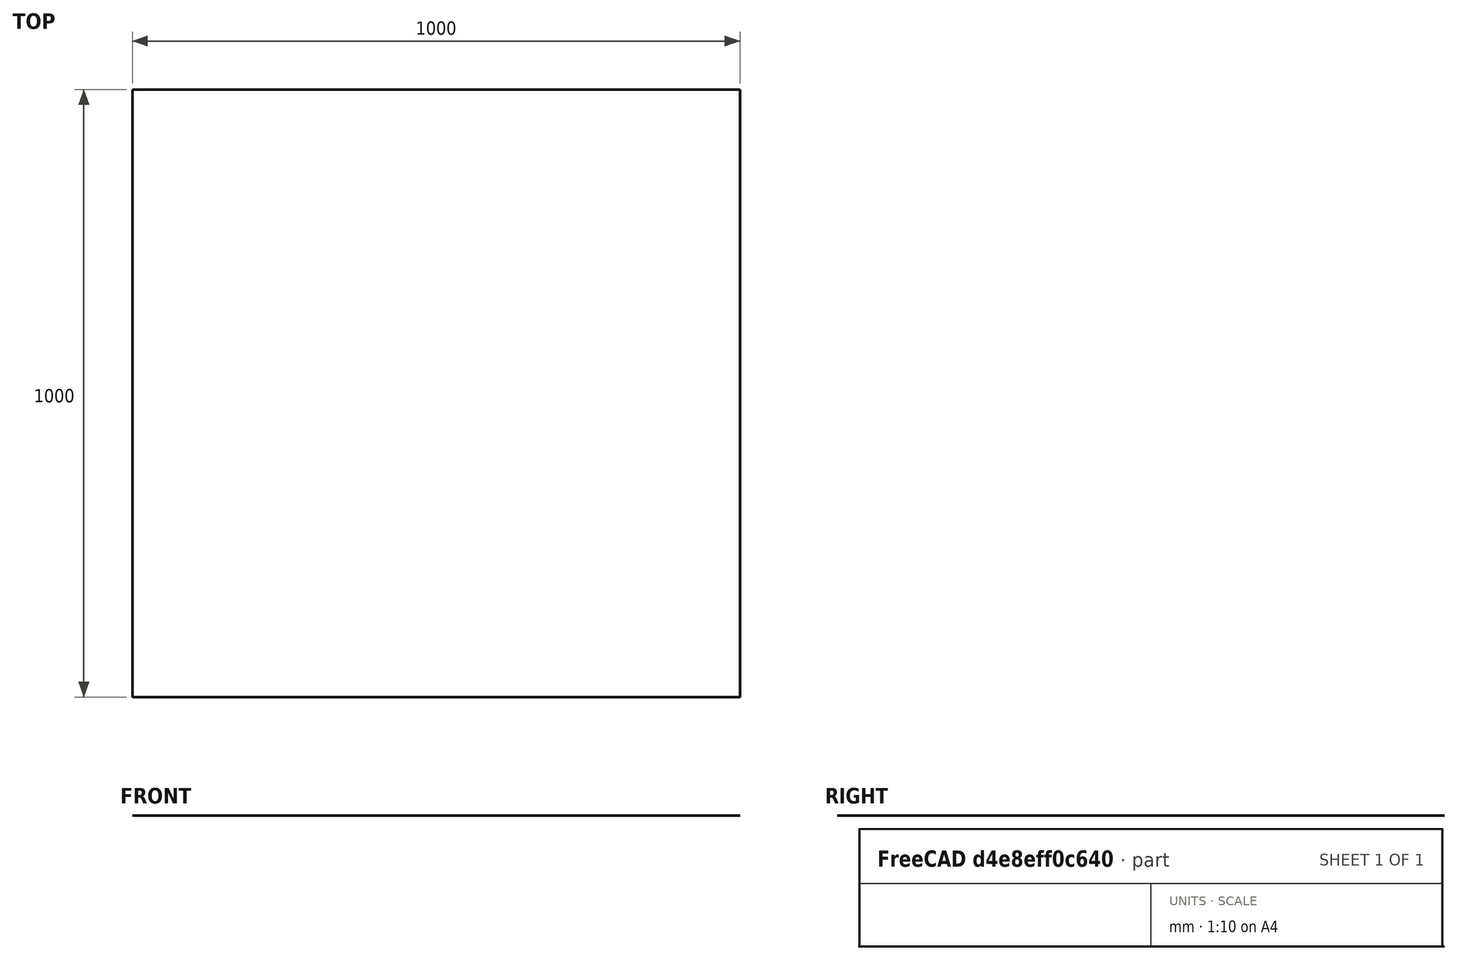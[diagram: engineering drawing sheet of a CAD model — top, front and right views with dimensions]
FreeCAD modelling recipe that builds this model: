
FCSTD DOCUMENT  (FreeCAD 0.17R11114 (Git))
Label: fridge_box
License: All rights reserved
LicenseURL: http://en.wikipedia.org/wiki/All_rights_reserved
objects: TechDraw::DrawViewDimension×26, Part::Part2DObjectPython×7, TechDraw::DrawViewDraft×4, Part::FeaturePython×3, TechDraw::DrawViewPart×3, Part::Compound×2, Part::Feature×2, TechDraw::DrawViewAnnotation×2, TechDraw::DrawSVGTemplate×1, App::DocumentObjectGroup×1, App::FeaturePython×1, TechDraw::DrawViewArch×1, App::DocumentObjectGroupPython×1, TechDraw::DrawPage×1
note: 15 computed .brp shape members not serialized (recipe doc carries the construction recipe); baked Part::Feature solids carry a one-line shape summary decoded from their .brp

FEATURE [Part::FeaturePython] fridge_box_door_01  # a2plus imported part (geometry in sourceFile) (typed FeaturePython)
  Placement = pos=(0,1e-12,0) rot=(0,0,1;0rad)
  fixedPosition = true
  sourceFile = fridge_box_door.fcstd
  timeLastImport = 1.49385e+09
  updateColors = true
FEATURE [Part::FeaturePython] fridge_box_panels_01  # a2plus imported part (geometry in sourceFile) (typed FeaturePython)
  fixedPosition = false
  sourceFile = A711_fridge_box_panels.fcstd
  timeLastImport = 1.49382e+09
  updateColors = true
FEATURE [Part::Compound] Compound
  Links = -> [fridge_box_door_01,fridge_box_panels_01]
FEATURE [TechDraw::DrawSVGTemplate] Template
  EditableTexts = 5cm_scaled_value=25cm; Architect_2=MARZIA FILATRELLA; Architect_3=MARCO FERRARA; Board_no=A712; Date=4.5.2017; Date_1=4.5.2017; Drawing_title_2=BOX FRIGO; Drawing_title_3=DISEGNI GENERALI; Filename=FRIDGE_BOX.FCSTD; Project_title_2=CASA VACANZE; Project_title_3=A SESTRI; Project_title_4=SCALA INTERNA; Revision=1.0; Scale=1:5; Sheet_of_sheets=3 DI 7 (nd); Size=A2; Version_1=1.0
  Height = 594
  Orientation = 0
  Width = 420
FEATURE [Part::Feature] Compound_cs  label="cs_hor_section"
  shape: bbox 610 x 720 x 3e-07 mm, 0 faces, 0 solids (baked)
FEATURE [Part::FeaturePython] fridge_box_door_02  # a2plus imported part (geometry in sourceFile) (typed FeaturePython)
  Placement = pos=(1865,1133,0) rot=(0,0,-1;1.5708rad)
  fixedPosition = false
  sourceFile = fridge_box_door.fcstd
  timeLastImport = 1.49385e+09
  updateColors = true
FEATURE [Part::Part2DObjectPython] Shape2DView001  # Draft 2D object (typed FeaturePython)
  Base = -> fridge_box_door_01
  FaceNumbers = [5]
  HiddenLines = false
  InPlace = true
  Projection = (0,0,1)
  ProjectionMode = 0
  SegmentLength = 0.05
  Tessellation = false
FEATURE [Part::Part2DObjectPython] Shape2DView  # Draft 2D object (typed FeaturePython)
  Base = -> fridge_box_door_02
  HiddenLines = false
  InPlace = true
  Projection = (0,0,1)
  ProjectionMode = 0
  SegmentLength = 0.05
  Tessellation = false
FEATURE [Part::Part2DObjectPython] Arc  # Draft 2D object (typed FeaturePython)
  FirstAngle = -90
  LastAngle = 0
  MakeFace = true
  Placement = pos=(1490,-357,0) rot=(0,0,1;0rad)
  Radius = 610
FEATURE [Part::Compound] Compound001  label="door_opening"
  Links = -> [Shape2DView001,Shape2DView,Arc]
FEATURE [App::DocumentObjectGroup] Group  label="utilities"
  Group = -> [fridge_box_door_02]
FEATURE [App::FeaturePython] Section  label="pl_hor_section"  # WARN: FeaturePython — macro-defined, semantics opaque (R4)
  Objects = -> [Compound]
  OnlySolids = true
  Placement = pos=(1810.65,0,1000) rot=(0,0,1;0rad)
FEATURE [TechDraw::DrawViewPart] View  label="plan"
  ArcCenterMarks = true
  CenterScale = 2
  Direction = (0,0,1)
  HardHidden = true
  HiddenWidth = 0.15
  HorizCenterLine = false
  IsoCount = 0
  IsoHidden = false
  IsoVisible = false
  IsoWidth = 0.3
  KeepLabel = false
  LineWidth = 0.5
  Rotation = 0
  Scale = 0.2
  ScaleType = 2
  SeamHidden = false
  SeamVisible = false
  ShowSectionLine = true
  SmoothHidden = false
  SmoothVisible = false
  Source = -> Compound_cs
  VertCenterLine = false
  X = 100
  Y = 275
FEATURE [TechDraw::DrawViewPart] View001  label="opening"
  ArcCenterMarks = true
  CenterScale = 2
  Direction = (0,0,1)
  HardHidden = false
  HiddenWidth = 0.15
  HorizCenterLine = false
  IsoCount = 0
  IsoHidden = false
  IsoVisible = false
  IsoWidth = 0.3
  KeepLabel = false
  LineWidth = 0.1
  Rotation = 0
  Scale = 0.2
  ScaleType = 2
  SeamHidden = false
  SeamVisible = false
  ShowSectionLine = true
  SmoothHidden = false
  SmoothVisible = false
  Source = -> Compound001
  VertCenterLine = false
  X = 100
  Y = 145.6
  expr: Y = View.Y - 2 * 64.700000000000003
  expr: X = View.X
FEATURE [TechDraw::DrawViewArch] ArchView  label="plan_all"
  AllOn = true
  FontSize = 12
  KeepLabel = false
  LineWidth = 0.05
  RenderMode = 0
  Rotation = 0
  Scale = 0.2
  ScaleType = 2
  ShowFill = false
  ShowHidden = true
  Source = -> Section
  Symbol = <blob: 2967 chars omitted>
  X = 35
  Y = 347.2
  expr: Y = View.Y + 2 * 36.100000000000001
  expr: X = View.X - 2 * 32.5
FEATURE [TechDraw::DrawViewDimension] Dimension
  Font = Arial
  Fontsize = 3
  FormatSpec = %value%
  KeepLabel = false
  LineWidth = 0.1
  MeasureType = 1
  References2D = -> [View]
  Rotation = 0
  ScaleType = 0
  Type = 2
  X = -48.5904
  Y = -6.90054
FEATURE [TechDraw::DrawViewDimension] Dimension001
  Font = Arial
  Fontsize = 3
  FormatSpec = %value%
  KeepLabel = false
  LineWidth = 0.1
  MeasureType = 1
  References2D = -> [View]
  Rotation = 0
  ScaleType = 0
  Type = 1
  X = 0.98199
  Y = -50.7245
FEATURE [TechDraw::DrawViewDimension] Dimension002
  Font = Arial
  Fontsize = 3
  FormatSpec = %value%
  KeepLabel = false
  LineWidth = 0.1
  MeasureType = 1
  References2D = -> [View]
  Rotation = 0
  ScaleType = 0
  Type = 1
  X = 5.21167
  Y = -86.0317
FEATURE [TechDraw::DrawViewDimension] Dimension003
  Font = Arial
  Fontsize = 3
  FormatSpec = %value%
  KeepLabel = false
  LineWidth = 0.1
  MeasureType = 1
  References2D = -> [View]
  Rotation = 0
  ScaleType = 0
  Type = 2
  X = -73.765
  Y = -8.8221
FEATURE [TechDraw::DrawViewDimension] Dimension004
  Font = Arial
  Fontsize = 3
  FormatSpec = %value%
  KeepLabel = false
  LineWidth = 0.1
  MeasureType = 1
  References2D = -> [View]
  Rotation = 0
  ScaleType = 0
  Type = 2
  X = 70.6336
  Y = -7.4087
FEATURE [Part::Feature] Compound_cs001  label="cs_vert_section"
  shape: bbox 630 x 3e-07 x 2050 mm, 0 faces, 0 solids (baked)
FEATURE [TechDraw::DrawViewPart] View002  label="section"
  ArcCenterMarks = true
  CenterScale = 2
  Direction = (0,-1,0)
  HardHidden = false
  HiddenWidth = 0.15
  HorizCenterLine = false
  IsoCount = 0
  IsoHidden = false
  IsoVisible = false
  IsoWidth = 0.3
  KeepLabel = false
  LineWidth = 0.5
  Rotation = 0
  Scale = 0.2
  ScaleType = 2
  SeamHidden = false
  SeamVisible = false
  ShowSectionLine = true
  SmoothHidden = false
  SmoothVisible = false
  Source = -> Compound_cs001
  VertCenterLine = false
  X = 260
  Y = 225
FEATURE [Part::Part2DObjectPython] Line  # Draft 2D object (typed FeaturePython)
  ChamferSize = 0
  Closed = false
  End = (2200,0,0)
  FilletRadius = 0
  Length = 810
  MakeFace = true
  Points = (2) [(1390,5.44968e-14,0),(2200,-2.0819e-14,0)]
  Start = (1390,0,0)
  Subdivisions = 0
FEATURE [Part::Part2DObjectPython] Rectangle  # Draft 2D object (typed FeaturePython)
  ChamferSize = 0
  Columns = 1
  FilletRadius = 25
  Height = 1441
  Length = 540
  MakeFace = false
  Placement = pos=(1525,0,50) rot=(1,0,0;1.5708rad)
  Rows = 1
FEATURE [App::DocumentObjectGroupPython] VisGroup  label="wr_fridge_front"  # scripted group (container) (typed FeaturePython)
  Group = -> [Line,Rectangle]
FEATURE [TechDraw::DrawViewDraft] DraftView  label="fridge_front"
  Direction = (0,1,0)
  FontSize = 12
  KeepLabel = false
  LineSpacing = 1
  LineStyle = Solid
  LineWidth = 0.1
  Rotation = 90
  Scale = 0.2
  ScaleType = 2
  Source = -> VisGroup
  Symbol = <svg\n xmlns="http://www.w3.org/2000/svg" version="1.1"\n xmlns:freecad="http://www.freecadweb.org/wiki/index.php?title=Svg_Namespace">\n<path id="Line_w0000"  d="M -0.0 -1390.0 L -0.0 -2200.0 " stroke="#000000" stroke-width="0.5 px" style="stroke-width:0.5;stroke-miterlimit:4;stroke-dasharray:none;fill:none;fill-rule: evenodd "/>\n<path id="Rectangle_w0000"  d="M 50.0 -1550.0 L 50.0 -2040.0 M 50.0 -2040.0 L 53.3493649054 -2052.5 L 62.5 -2061.65063509 L 75.0 -2065.0 L 1466.0 -2065.0 M 1466.0 -2065.0 L 1478.5 -2061.65063509 L 1487.65063509 -2052.5 L 1491.0 -2040.0 L 1491.0 -1550.0 M 1491.0 -1550.0 L 1487.65063509 -1537.5 L 1478.5 -1528.34936491 L 1466.0 -1525.0 L 75.0 -1525.0 M 75.0 -1525.0 L 62.5 -1528.34936491 L 53.3493649054 -1537.5 L 50.0 -1550.0 " stroke="#000000" stroke-width="0.5 px" style="stroke-width:0.5;stroke-miterlimit:4;stroke-dasharray:none;fill:none;fill-rule: evenodd "/>\n\n</svg>
  X = 113.6
  Y = 250.6
  expr: Y = View002.Y + 2 * 12.800000000000001
  expr: X = View002.X - 2 * 73.200000000000003
FEATURE [Part::Part2DObjectPython] Shape2DView002  label="wr_floor_front"  # Draft 2D object (typed FeaturePython)
  Base = -> fridge_box_door_01
  HiddenLines = false
  InPlace = true
  Placement = pos=(3e-12,-366,2.23517e-05) rot=(0.57735,0.57735,-0.57735;2.0944rad)
  Projection = (0,-1,5.9605e-08)
  ProjectionMode = 0
  SegmentLength = 0.05
  Tessellation = false
FEATURE [TechDraw::DrawViewDraft] DraftView001  label="door_front"
  Direction = (0,-1,0)
  FontSize = 12
  KeepLabel = false
  LineSpacing = 1
  LineStyle = 3,1
  LineWidth = 0.1
  Rotation = -90
  Scale = 0.2
  ScaleType = 2
  Source = -> Shape2DView002
  Symbol = <svg\n xmlns="http://www.w3.org/2000/svg" version="1.1"\n xmlns:freecad="http://www.freecadweb.org/wiki/index.php?title=Svg_Namespace">\n<path id="Shape2DView002_nwe0000"  d="M -1687.4733916 -1490.0 L -2100.0 -1912.58825684 " stroke="#000000" stroke-width="0.5 px" style="stroke-width:0.5;stroke-miterlimit:4;stroke-dasharray:15.0,5.0;fill:none;fill-rule: evenodd "/>\n<path id="Shape2DView002_nwe0001"  d="M -2100.0 -1912.58825684 L -2100.0 -2100.0 " stroke="#000000" stroke-width="0.5 px" style="stroke-width:0.5;stroke-miterlimit:4;stroke-dasharray:15.0,5.0;fill:none;fill-rule: evenodd "/>\n<path id="Shape2DView002_nwe0002"  d="M -2100.0 -2100.0 L -4.99999999987 -2100.0 " stroke="#000000" stroke-width="0.5 px" style="stroke-width:0.5;stroke-miterlimit:4;stroke-dasharray:15.0,5.0;fill:none;fill-rule: evenodd "/>\n<path id="Shape2DView002_nwe0003"  d="M -4.99999999987 -2100.0 L -4.99999999987 -1490.0 " stroke="#000000" stroke-width="0.5 px" style="stroke-width:0.5;stroke-miterlimit:4;stroke-dasharray:15.0,5.0;fill:none;fill-rule: evenodd "/>\n<path id="Shape2DView002_nwe0004"  d="M -4.99999999987 -1490.0 L -1687.4733916 -1490.0 " stroke="#000000" stroke-width="0.5 px" style="stroke-width:0.5;stroke-miterlimit:4;stroke-dasharray:15.0,5.0;fill:none;fill-rule: evenodd "/>\n\n</svg>
  X = 52
  Y = 292.5
  expr: Y = View002.Y + 2 * 33.75
  expr: X = View002.X - 2 * 104
FEATURE [TechDraw::DrawViewDraft] DraftView002  label="floor_front"
  Direction = (0,1,0)
  FontSize = 12
  KeepLabel = false
  LineSpacing = 1
  LineStyle = Solid
  LineWidth = 0.7
  Rotation = 90
  Scale = 0.2
  ScaleType = 2
  Source = -> Line
  Symbol = <svg\n xmlns="http://www.w3.org/2000/svg" version="1.1"\n xmlns:freecad="http://www.freecadweb.org/wiki/index.php?title=Svg_Namespace">\n<path id="Line_w0000"  d="M -0.0 -1390.0 L -0.0 -2200.0 " stroke="#000000" stroke-width="3.5 px" style="stroke-width:3.5;stroke-miterlimit:4;stroke-dasharray:none;fill:none;fill-rule: evenodd "/>\n\n</svg>
  X = 262.4
  Y = 101.5
  expr: Y = View002.Y - 2 * 61.75
  expr: X = View002.X + 2 * 1.2
FEATURE [TechDraw::DrawViewDimension] Dimension005
  Font = Arial
  Fontsize = 3
  FormatSpec = %value%
  KeepLabel = false
  LineWidth = 0.1
  MeasureType = 1
  References2D = -> [View002]
  Rotation = 0
  ScaleType = 0
  Type = 2
  X = 70.9971
  Y = -6.86949
FEATURE [TechDraw::DrawViewDimension] Dimension006
  Font = Arial
  Fontsize = 3
  FormatSpec = %value%
  KeepLabel = false
  LineWidth = 0.1
  MeasureType = 1
  References2D = -> [View002]
  Rotation = 0
  ScaleType = 0
  Type = 2
  X = -72.0802
  Y = -3.8812
FEATURE [TechDraw::DrawViewDimension] Dimension007
  Font = Arial
  Fontsize = 3
  FormatSpec = %value%
  KeepLabel = false
  LineWidth = 0.1
  MeasureType = 1
  References2D = -> [View002]
  Rotation = 0
  ScaleType = 0
  Type = 2
  X = -71.7791
  Y = -141.166
FEATURE [TechDraw::DrawViewDimension] Dimension008
  Font = Arial
  Fontsize = 3
  FormatSpec = %value%
  KeepLabel = false
  LineWidth = 0.1
  MeasureType = 1
  References2D = -> [View002]
  Rotation = 0
  ScaleType = 0
  Type = 2
  X = -71.319
  Y = -184.082
FEATURE [TechDraw::DrawViewDimension] Dimension009
  Font = Arial
  Fontsize = 3
  FormatSpec = %value%
  KeepLabel = false
  LineWidth = 0.1
  MeasureType = 1
  References2D = -> [View002]
  Rotation = 0
  ScaleType = 0
  Type = 2
  X = 39.2242
  Y = -180.668
FEATURE [TechDraw::DrawViewDimension] Dimension010
  Font = Arial
  Fontsize = 3
  FormatSpec = %value%
  KeepLabel = false
  LineWidth = 0.1
  MeasureType = 1
  References2D = -> [View002]
  Rotation = 0
  ScaleType = 0
  Type = 2
  X = -2.00778
  Y = -140.108
FEATURE [TechDraw::DrawViewDimension] Dimension011
  Font = Arial
  Fontsize = 3
  FormatSpec = %value%
  KeepLabel = false
  LineWidth = 0.1
  MeasureType = 1
  References2D = -> [View002]
  Rotation = 0
  ScaleType = 0
  Type = 2
  X = -46.3155
  Y = 3.02463
FEATURE [TechDraw::DrawViewDimension] Dimension012
  Font = Arial
  Fontsize = 3
  FormatSpec = %value%
  KeepLabel = false
  LineWidth = 0.1
  MeasureType = 1
  References2D = -> [View002]
  Rotation = 0
  ScaleType = 0
  Type = 1
  X = -2.37536
  Y = 177.855
FEATURE [TechDraw::DrawViewDimension] Dimension013
  Font = Arial
  Fontsize = 3
  FormatSpec = %value%
  KeepLabel = false
  LineWidth = 0.1
  MeasureType = 1
  References2D = -> [View002]
  Rotation = 0
  ScaleType = 0
  Type = 1
  X = 42.6774
  Y = -217.597
FEATURE [TechDraw::DrawViewDimension] Dimension015
  Font = Arial
  Fontsize = 3
  FormatSpec = %value%
  KeepLabel = false
  LineWidth = 0.1
  MeasureType = 1
  References2D = -> [View002]
  Rotation = 0
  ScaleType = 0
  Type = 1
  X = -36.607
  Y = -134.591
FEATURE [TechDraw::DrawViewDimension] Dimension016
  Font = Arial
  Fontsize = 3
  FormatSpec = %value%
  KeepLabel = false
  LineWidth = 0.1
  MeasureType = 1
  References2D = -> [View002]
  Rotation = 0
  ScaleType = 0
  Type = 1
  X = 1.79472
  Y = -174.959
FEATURE [TechDraw::DrawViewDimension] Dimension017
  Font = Arial
  Fontsize = 3
  FormatSpec = %value%
  KeepLabel = false
  LineWidth = 0.1
  MeasureType = 1
  References2D = -> [View002]
  Rotation = 0
  ScaleType = 0
  Type = 1
  X = -1.30259
  Y = -217.577
FEATURE [TechDraw::DrawViewDimension] Dimension018
  Font = Arial
  Fontsize = 3
  FormatSpec = %value%
  KeepLabel = false
  LineWidth = 0.1
  MeasureType = 1
  References2D = -> [View002]
  Rotation = 0
  ScaleType = 0
  Type = 1
  X = -39.5846
  Y = -217.577
FEATURE [TechDraw::DrawViewDimension] Dimension019
  Font = Arial
  Fontsize = 3
  FormatSpec = %value%
  KeepLabel = false
  LineWidth = 0.1
  MeasureType = 1
  References2D = -> [View002]
  Rotation = 0
  ScaleType = 0
  Type = 2
  X = -37.6838
  Y = 188.97
FEATURE [TechDraw::DrawViewDimension] Dimension020
  Font = Arial
  Fontsize = 3
  FormatSpec = %value%
  KeepLabel = false
  LineWidth = 0.1
  MeasureType = 1
  References2D = -> [View002]
  Rotation = 0
  ScaleType = 0
  Type = 2
  X = 46.246
  Y = 210.646
FEATURE [TechDraw::DrawViewDimension] Dimension021
  Font = Arial
  Fontsize = 3
  FormatSpec = %value%
  KeepLabel = false
  LineWidth = 0.1
  MeasureType = 1
  References2D = -> [View002]
  Rotation = 0
  ScaleType = 0
  Type = 2
  X = 9.45795
  Y = -110.434
FEATURE [TechDraw::DrawViewDimension] Dimension023
  Font = Arial
  Fontsize = 3
  FormatSpec = %value%
  KeepLabel = false
  LineWidth = 0.1
  MeasureType = 1
  References2D = -> [View002]
  Rotation = 0
  ScaleType = 0
  Type = 2
  X = -30.2499
  Y = -149.812
FEATURE [TechDraw::DrawViewDimension] Dimension024
  Font = Arial
  Fontsize = 3
  FormatSpec = %value%
  KeepLabel = false
  LineWidth = 0.1
  MeasureType = 1
  References2D = -> [View002]
  Rotation = 0
  ScaleType = 0
  Type = 2
  X = 9.45521
  Y = -188.359
FEATURE [TechDraw::DrawViewAnnotation] Annotation  label="fridge_anno"
  Font = Arial
  KeepLabel = false
  LineSpace = 120
  MaxWidth = -1
  Rotation = 0
  ScaleType = 0
  Text = FRIGORIFERO DA INCASSO | INDESIT IN D 2413 | Altezza: cm 144.1 | Larghezza: cm 54.0 | Profondità: cm 54.5
  TextSize = 3
  TextStyle = 0
  X = 238.5
  Y = 192.5
  expr: Y = DraftView.Y - 58.100000000000001
  expr: X = DraftView.X + 124.90000000000001
FEATURE [TechDraw::DrawViewDimension] Dimension025
  Font = Arial
  Fontsize = 3
  FormatSpec = %value%
  KeepLabel = false
  LineWidth = 0.1
  MeasureType = 1
  References2D = -> [View]
  Rotation = 0
  ScaleType = 0
  Type = 1
  X = 47.3434
  Y = -40.1154
FEATURE [TechDraw::DrawViewDimension] Dimension026
  Font = Arial
  Fontsize = 3
  FormatSpec = %value%
  KeepLabel = false
  LineWidth = 0.1
  MeasureType = 1
  References2D = -> [View]
  Rotation = 0
  ScaleType = 0
  Type = 2
  X = 38.2597
  Y = -60.1267
FEATURE [TechDraw::DrawViewDimension] Dimension027
  Font = Arial
  Fontsize = 3
  FormatSpec = %value%
  KeepLabel = false
  LineWidth = 0.1
  MeasureType = 1
  References2D = -> [View]
  Rotation = 0
  ScaleType = 0
  Type = 2
  X = 42.6653
  Y = 59.4804
FEATURE [Part::Part2DObjectPython] Rectangle001  # Draft 2D object (typed FeaturePython)
  ChamferSize = 0
  Columns = 1
  FilletRadius = 25
  Height = 545
  Length = 540
  MakeFace = false
  Placement = pos=(1525,-337,1050) rot=(0,0,1;0rad)
  Rows = 1
FEATURE [TechDraw::DrawViewDraft] DraftView003  label="fridge_plan"
  Direction = (0,0,0)
  FontSize = 12
  KeepLabel = false
  LineSpacing = 1
  LineStyle = Solid
  LineWidth = 0.1
  Rotation = 0
  Scale = 0.2
  ScaleType = 2
  Source = -> Rectangle001
  Symbol = <svg\n xmlns="http://www.w3.org/2000/svg" version="1.1"\n xmlns:freecad="http://www.freecadweb.org/wiki/index.php?title=Svg_Namespace">\n<path id="Rectangle001_w0000"  d="M 1550.0 -337.0 L 2040.0 -337.0 A 25 25 0 0 1 2065 -312L 2065.0 183.0 A 25 25 0 0 1 2040 208L 1550.0 208.0 A 25 25 0 0 1 1525 183L 1525.0 -312.0 A 25 25 0 0 1 1550 -337" stroke="#000000" stroke-width="0.5 px" style="stroke-width:0.5;stroke-miterlimit:4;stroke-dasharray:none;fill:none;fill-rule: evenodd "/>\n\n</svg>
  X = 45.8
  Y = 319.8
  expr: Y = View.Y + 44.799999999999997
  expr: X = View.X - 54.200000000000003
FEATURE [TechDraw::DrawViewAnnotation] Annotation001
  Font = Arial
  KeepLabel = false
  LineSpace = 120
  MaxWidth = -1
  Rotation = 0
  ScaleType = 0
  Text = I giunti e le connessioni tra i pannelli dovranno essere definiti in opera  | attraverso incastri e piastre metalliche al fine di garantire la massima | stabilità e sicurezza.
  TextSize = 3
  TextStyle = 0
  X = 40.4138
  Y = 40.7364
FEATURE [TechDraw::DrawPage] Page
  ProjectionType = 0
  Template = -> Template
  Views = -> [View,View001,ArchView,Dimension,Dimension001,Dimension002,Dimension003,Dimension004,View002,DraftView,DraftView001,DraftView002,Dimension005,Dimension006,Dimension007,Dimension008,Dimension009,Dimension010,Dimension011,Dimension012,Dimension013,Dimension015,Dimension016,Dimension017,Dimension018,Dimension019,Dimension020,Dimension021,Dimension023,Dimension024,Annotation,Dimension025,Dimension026,+3 more]
